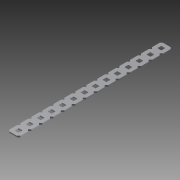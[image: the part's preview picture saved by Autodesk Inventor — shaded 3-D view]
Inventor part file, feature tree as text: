
AUTODESK INVENTOR PART (.ipt)
format: ipt  version: 2014 SP1 (Build 180222100, 222)  size: 536,576 bytes
history: native  units: in
note: dims shown in document units (in); Inventor stores cm internally (conversion verified against a paired STEP export)
features: other x1, imported_body x1, extrude x1, sketch x1
ambient origin geometry x8: Origin, YZ Plane, XZ Plane, XY Plane, X Axis, Y Axis, Z Axis, Center Point
bodies: Body1 (feature_tree)
feature tree (4):
  parser-record x1  (decoder bookkeeping rows leaked as tree rows — omitted from the tree; the rows remain in map.json)
  imported_body  "Base1"
  extrude  "Extrusion1"  Depth=1.0in TaperAngle=0.0deg
  sketch  "Sketch1"  dims[d0=7.0in d1=1.0in d2=0.0in]
